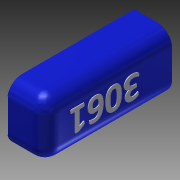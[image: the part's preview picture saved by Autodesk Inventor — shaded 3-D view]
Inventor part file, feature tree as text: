
AUTODESK INVENTOR PART (.ipt)
format: ipt  version: 2013 (Build 170138000, 138)  size: 361,472 bytes
history: native  units: in
note: dims shown in document units (in); Inventor stores cm internally (conversion verified against a paired STEP export)
features: extrude x4, reference x4, sketch x3, fillet x1, projected_geometry x1
ambient origin geometry x8: Origin, YZ Plane, XZ Plane, XY Plane, X Axis, Y Axis, Z Axis, Center Point
bodies: Solid1 (feature_tree)
feature tree (13):
  sketch  "Sketch1"  dims[d0=0.0625in d1=0.0in d3=1.0in]
  extrude  "Extrusion1"  Depth=1.0in
  extrude  "Extrusion2"  Depth=0.0625in
  extrude  "Extrusion3"  Depth=0.0625in TaperAngle=0.0deg
  fillet  "Fillet1"  Radius=1.3125in
  extrude  "Extrusion4"  Depth=6.0in
  reference  "Reference4"
  reference  "Reference5"
  sketch  "Sketch2"  dims[d7=1.0in d9=0.0625in]
  sketch  "Sketch3"  dims[d10=11.25in d11=0.0in d12=0.0625in d13=0.0in d14=1.3125in d15=6.0in d17=1.0in d18=0.0625in d19=0.0in d20=0.0625in d21=0.0625in]
  reference  "Reference6"
  projected_geometry  "Projected Loop1"
  reference  "Reference7"
